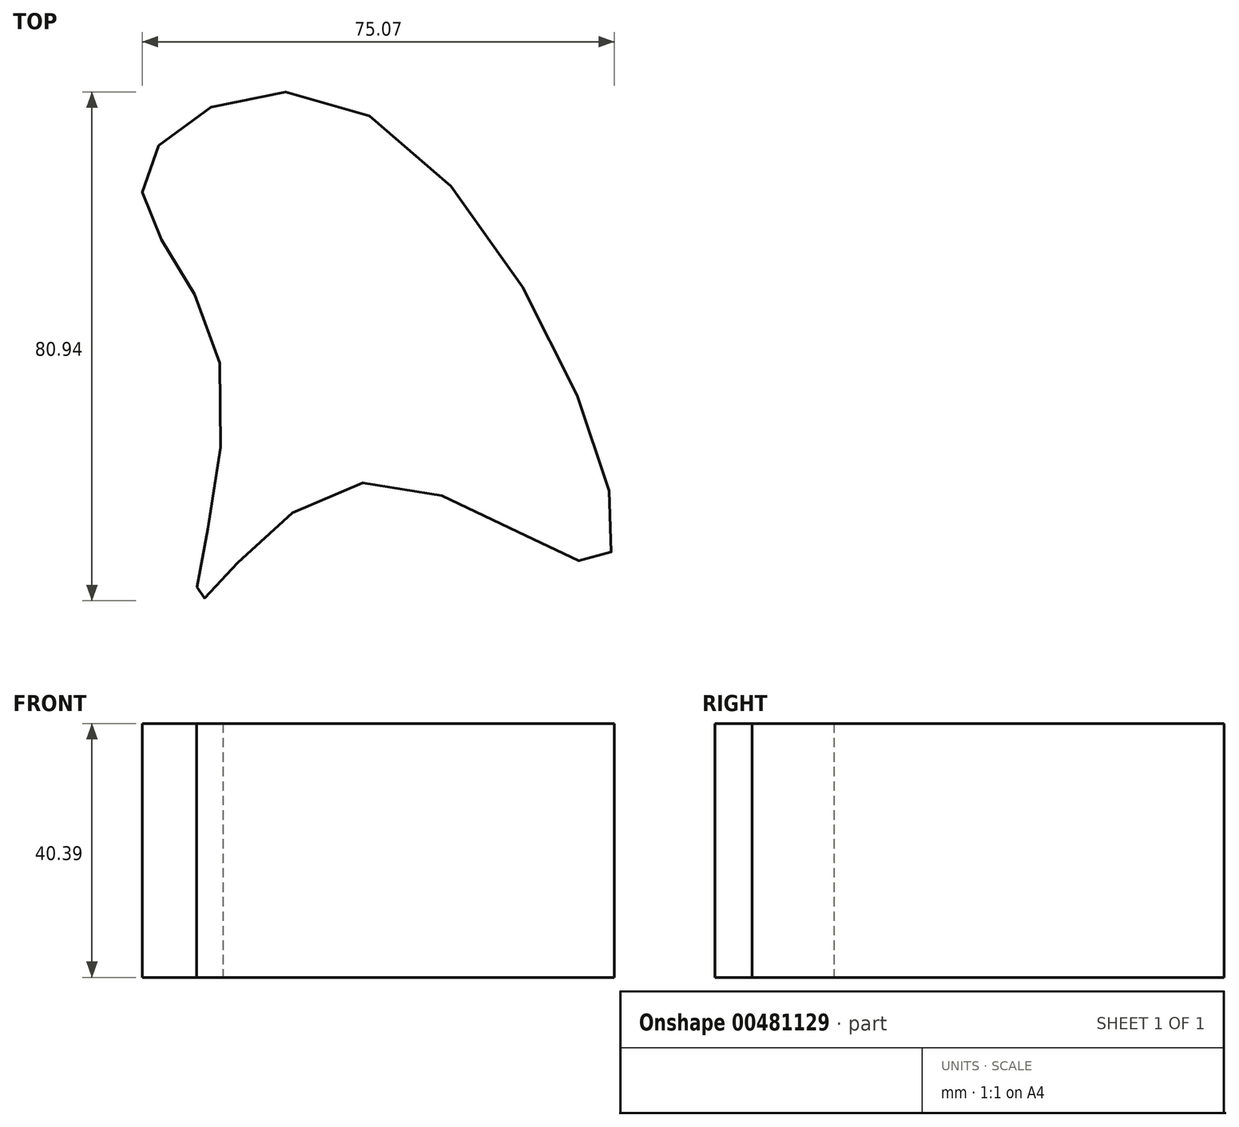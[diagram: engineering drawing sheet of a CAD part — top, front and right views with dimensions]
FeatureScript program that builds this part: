
annotation { "Feature Type Name" : "Feature", "Feature Type Description" : "" }
export const myFeature = defineFeature(function(context is Context, id is Id, definition is map)
    precondition{}
    {
        {
            var Q0;
            Q0=qCreatedBy(makeId("Top.planeOp"),FACE);
            var sketch = newSketch(context, id + "F0", { "sketchPlane" : qUnion([Q0])});
            skFitSpline(sketch, "E0", {"points": [v(-22.66, 0) * mm, v(-34.78, 29.8) * mm, v(0, 39.96) * mm, v(38.88, -31.16) * mm, v(0, -19.05) * mm, v(-25.99, -37.8) * mm, v(-22.66, 0) * mm]});
            skSolve(sketch);
        }
        {
            var Q0;
            Q0 = qSketchRegion(id + "F0", true);
            extrude(context, id + "F1", {"entities" : qUnion([Q0]), "depth" : 40.4 * mm});
        }
    });
